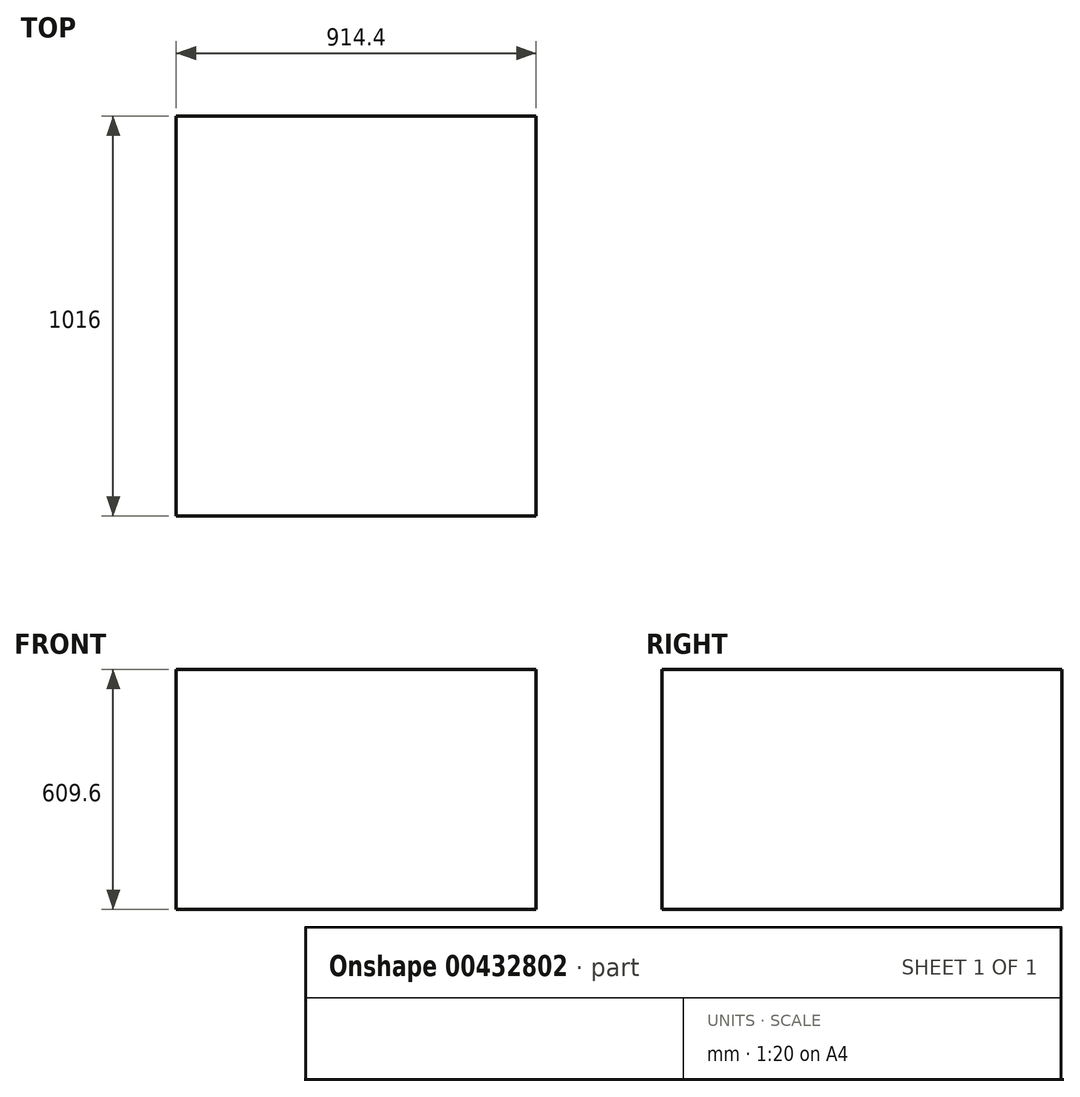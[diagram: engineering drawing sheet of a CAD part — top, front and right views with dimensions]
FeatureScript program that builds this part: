
annotation { "Feature Type Name" : "Feature", "Feature Type Description" : "" }
export const myFeature = defineFeature(function(context is Context, id is Id, definition is map)
    precondition{}
    {
        {
            var Q0;
            Q0=qCreatedBy(makeId("Top.planeOp"),FACE);
            var sketch = newSketch(context, id + "F0", { "sketchPlane" : qUnion([Q0])});
            skLineSegment(sketch, "E0.bottom", {"start": v(457.2, -508) * mm, "end": v(-457.2, -508) * mm});
            skLineSegment(sketch, "E0.top", {"start": v(457.2, 508) * mm, "end": v(-457.2, 508) * mm});
            skLineSegment(sketch, "E0.left", {"start": v(457.2, -508) * mm, "end": v(457.2, 508) * mm});
            skLineSegment(sketch, "E0.right", {"start": v(-457.2, -508) * mm, "end": v(-457.2, 508) * mm});
            skPoint(sketch, "E0.middle", {"position": v(0, 0) * mm});
            skSolve(sketch);
        }
        {
            var Q0;
            Q0 = qSketchRegion(id + "F0", true);
            extrude(context, id + "F1", {"entities" : qUnion([Q0]), "depth" : 609.6 * mm});
        }
    });
